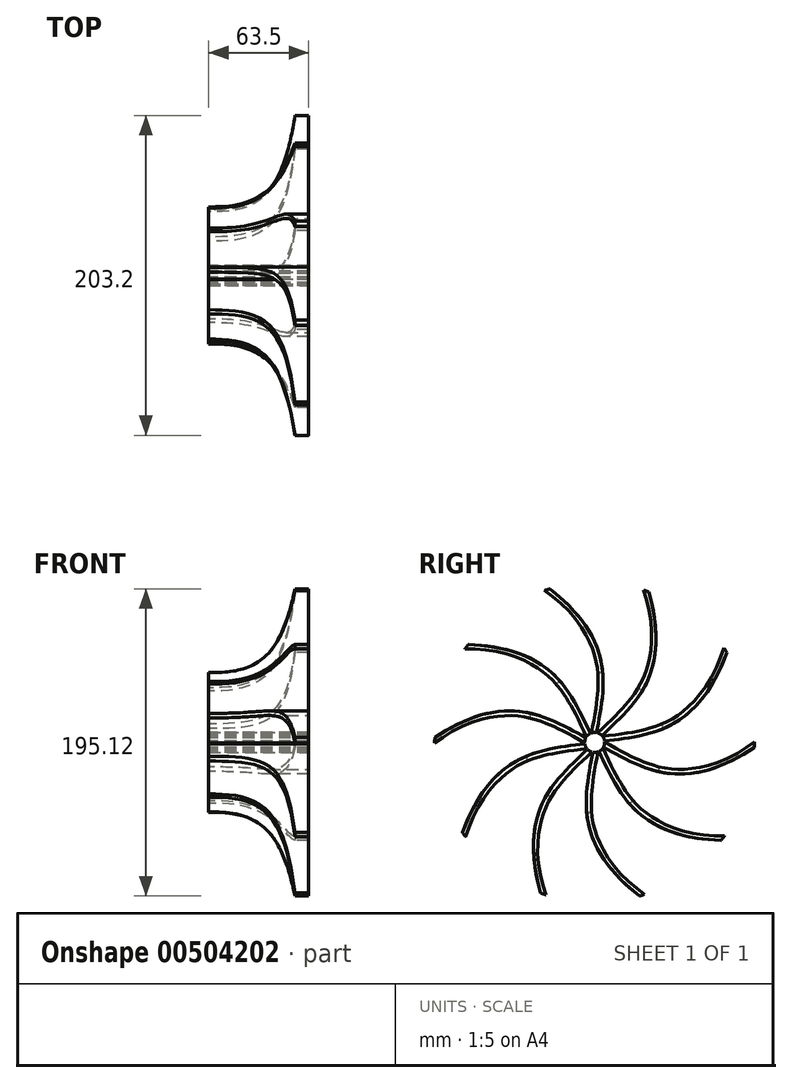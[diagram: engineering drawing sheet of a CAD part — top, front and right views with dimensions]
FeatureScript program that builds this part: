
annotation { "Feature Type Name" : "Feature", "Feature Type Description" : "" }
export const myFeature = defineFeature(function(context is Context, id is Id, definition is map)
    precondition{}
    {
        {
            var Q0;
            Q0=qCreatedBy(makeId("Front.planeOp"),FACE);
            var sketch = newSketch(context, id + "F0", { "sketchPlane" : qUnion([Q0])});
            skLineSegment(sketch, "E0", {"start": v(-7.94, 101.6) * mm, "end": v(-7.94, 12.7) * mm, "construction": true});
            skLineSegment(sketch, "E1", {"start": v(-7.94, 12.7) * mm, "end": v(-73.03, 12.7) * mm, "construction": true});
            skLineSegment(sketch, "E2", {"start": v(-73.03, 12.7) * mm, "end": v(-73.03, 3.17) * mm});
            skLineSegment(sketch, "E3", {"start": v(-73.03, 3.17) * mm, "end": v(0, 3.18) * mm});
            skLineSegment(sketch, "E4", {"start": v(0, 3.18) * mm, "end": v(0, 101.6) * mm});
            skLineSegment(sketch, "E5", {"start": v(0, 101.6) * mm, "end": v(-7.94, 101.6) * mm});
            skLineSegment(sketch, "E6", {"start": v(0, 0) * mm, "end": v(-82.55, 0) * mm, "construction": true});
            skFitSpline(sketch, "E7", {"points": [v(-73.03, 12.7) * mm, v(-28.58, 28.58) * mm, v(-17.46, 44.45) * mm, v(-12.7, 60.33) * mm, v(-7.94, 98.43) * mm], "startDerivative": vector(149.32, 0) * mm, "endDerivative": vector(0, 182.1) * mm});
            skLineSegment(sketch, "E8", {"start": v(-7.94, 98.43) * mm, "end": v(-7.94, 101.6) * mm});
            skSolve(sketch);
        }
        {
            var Q0;
            Q0=sQuery(id+"F0.wireOp",EDGE,"E2");
            var Q1;
            Q1=sQuery(id+"F0.wireOp",EDGE,"E3");
            var Q2;
            Q2=sQuery(id+"F0.wireOp",EDGE,"E4");
            var Q3;
            Q3=sQuery(id+"F0.wireOp",EDGE,"E5");
            var Q4;
            Q4=sQuery(id+"F0.wireOp",EDGE,"E8");
            var Q5;
            Q5=sQuery(id+"F0.wireOp",EDGE,"E7");
            var Q6;
            Q6=sQuery(id+"F0.wireOp",EDGE,"E6");
            revolve(context, id + "F1", {"bodyType" : ToolBodyType.SURFACE, "surfaceEntities" : qUnion([Q0, Q1, Q2, Q3, Q4, Q5]), "axis" : qUnion([Q6]), "revolveType" : RevolveType.FULL});
        }
        {
            var Q0;
            Q0=makeQuery(id+"F1.opRevolve","SWEPT_FACE",FACE,{"disambiguationData":[OSD([sQuery(id+"F0.wireOp",EDGE,"E2")])]});
            cPlane(context, id + "F2", {"entities" : qUnion([Q0]), "cplaneType" : CPlaneType.OFFSET, "offset" : 3.17 * mm, "width" : 152.4 * mm, "height" : 152.4 * mm});
        }
        {
            var Q0;
            Q0=qCreatedBy(id+"F2.planeOp",FACE);
            var sketch = newSketch(context, id + "F3", { "sketchPlane" : qUnion([Q0])});
            skCircle(sketch, "E9.0", {"center": v(0, 0) * mm, "radius": 12.7 * mm, "construction": true});
            skCircle(sketch, "E10.0", {"center": v(0, 0) * mm, "radius": 101.6 * mm, "construction": true});
            skCircle(sketch, "E11.0", {"center": v(0, 0) * mm, "radius": 98.43 * mm, "construction": true});
            skFitSpline(sketch, "E12", {"points": [v(0, 0) * mm, v(5.08, 31.75) * mm, v(-38.1, 104.78) * mm], "startDerivative": vector(12, 75) * mm, "endDerivative": vector(-200.06, 138.5) * mm});
            skLineSegment(sketch, "E13", {"start": v(-130.62, 0) * mm, "end": v(132.26, 0) * mm, "construction": true});
            skLineSegment(sketch, "E14", {"start": v(0, 122.97) * mm, "end": v(0, -146.11) * mm, "construction": true});
            skFitSpline(sketch, "E15.0", {"points": [v(-3.14, 0.5) * mm, v(-2.62, 3.7) * mm, v(-1.68, 8.54) * mm, v(-0.38, 15.22) * mm, v(0.54, 20.39) * mm, v(1.2, 24.86) * mm, v(1.63, 28.57) * mm, v(1.88, 31.4) * mm, v(2.07, 34.32) * mm, v(2.2, 38.27) * mm, v(2.08, 43.36) * mm, v(1.29, 49.7) * mm, v(-0.34, 56.29) * mm, v(-3, 63.16) * mm, v(-8.2, 72.72) * mm, v(-18.41, 85.48) * mm, v(-31.7, 96.48) * mm, v(-39.9, 102.16) * mm]});
            skLineSegment(sketch, "E16", {"start": v(-39.9, 102.16) * mm, "end": v(-38.1, 104.78) * mm});
            skLineSegment(sketch, "E17", {"start": v(-3.14, 0.5) * mm, "end": v(0, 0) * mm});
            skSolve(sketch);
        }
        {
            var Q0;
            Q0=makeQuery(id+"F3.imprint","IMPRINT",FACE,{"disambiguationData":[TD([[makeQuery(id+"F3.imprint","IMPRINT",EDGE,{"derivedFrom":sQuery(id+"F3.wireOp",EDGE,"E12")}),1.0]])]});
            var Q1;
            Q1=makeQuery(id+"F1.opRevolve","SWEPT_FACE",FACE,{"disambiguationData":[OSD([sQuery(id+"F0.wireOp",EDGE,"E8")])]});
            extrude(context, id + "F4", {"entities" : qUnion([Q0]), "endBoundEntityFace" : qUnion([Q1]), "depth" : 63.5 * mm});
        }
        {
            var Q0;
            Q0=qCreatedBy(makeId("Front.planeOp"),FACE);
            var sketch = newSketch(context, id + "F5", { "sketchPlane" : qUnion([Q0])});
            skFitSpline(sketch, "E18.0", {"points": [v(-69.85, 0.5) * mm, v(-69.85, 3.57) * mm, v(-69.85, 8.13) * mm, v(-69.85, 14.4) * mm, v(-69.85, 19.26) * mm, v(-69.85, 24.35) * mm, v(-69.85, 28.86) * mm, v(-69.85, 32.64) * mm, v(-69.85, 36.58) * mm, v(-69.85, 41.79) * mm, v(-69.85, 48.45) * mm, v(-69.85, 57.84) * mm, v(-69.85, 70.48) * mm, v(-69.85, 86.87) * mm, v(-69.85, 98.48) * mm, v(-69.85, 104.42) * mm]});
            skLineSegment(sketch, "E19.0", {"start": v(-6.35, 102.16) * mm, "end": v(-69.85, 102.16) * mm});
            skFitSpline(sketch, "E20", {"points": [v(-73.03, 44.45) * mm, v(-50.8, 46.04) * mm, v(-30.16, 58.74) * mm, v(-17.46, 88.9) * mm, v(-12.7, 117.48) * mm], "startDerivative": vector(83.73, 0) * mm, "endDerivative": vector(18.36, 110.14) * mm});
            skLineSegment(sketch, "E21", {"start": v(-73.03, 44.45) * mm, "end": v(-73.03, 117.47) * mm});
            skLineSegment(sketch, "E22", {"start": v(-73.03, 117.48) * mm, "end": v(-12.7, 117.48) * mm});
            skLineSegment(sketch, "E23", {"start": v(0, 0) * mm, "end": v(-127, 0) * mm, "construction": true});
            skSolve(sketch);
        }
        {
            var Q0;
            {var subQ0=sQuery(id+"F5.wireOp",EDGE,"E19.0");var subQ1=sQuery(id+"F5.wireOp",EDGE,"E18.0");var subQ2=makeQuery(id+"F5.imprint","INTERSECT",VERTEX,{"derivedFrom":[subQ1,subQ0]});Q0=makeQuery(id+"F5.imprint","IMPRINT",FACE,{"disambiguationData":[TD([[makeQuery(id+"F5.imprint","IMPRINT",EDGE,{"disambiguationData":[TD([[subQ2,1.0]])],"derivedFrom":subQ1}),-1.0]])]});}
            var Q1;
            {var subQ4=sQuery(id+"F5.wireOp",EDGE,"E21");Q1=makeQuery(id+"F5.imprint","IMPRINT",FACE,{"disambiguationData":[TD([[makeQuery(id+"F5.imprint","IMPRINT",EDGE,{"derivedFrom":subQ4}),-1.0]])]});}
            var Q2;
            Q2=sQuery(id+"F5.wireOp",EDGE,"E23");
            revolve(context, id + "F6", {"operationType" : NewBodyOperationType.REMOVE, "entities" : qUnion([Q0, Q1]), "axis" : qUnion([Q2]), "revolveType" : RevolveType.FULL, "oppositeDirection" : true});
        }
        {
            var Q0;
            Q0=qCreatedBy(makeId("Front.planeOp"),FACE);
            var sketch = newSketch(context, id + "F7", { "sketchPlane" : qUnion([Q0])});
            skLineSegment(sketch, "E24.bottom", {"start": v(-76.2, 6.35) * mm, "end": v(25.4, 6.35) * mm});
            skLineSegment(sketch, "E24.top", {"start": v(-76.2, 101.6) * mm, "end": v(25.4, 101.6) * mm});
            skLineSegment(sketch, "E24.left", {"start": v(-76.2, 101.6) * mm, "end": v(-76.2, 6.35) * mm});
            skLineSegment(sketch, "E24.right", {"start": v(25.4, 101.6) * mm, "end": v(25.4, 6.35) * mm});
            skLineSegment(sketch, "E25", {"start": v(0, 0) * mm, "end": v(-101.6, 0) * mm, "construction": true});
            skSolve(sketch);
        }
        {
            var Q0;
            Q0=makeQuery(id+"F7.imprint","IMPRINT",FACE,{"disambiguationData":[TD([[makeQuery(id+"F7.imprint","IMPRINT",EDGE,{"derivedFrom":sQuery(id+"F7.wireOp",EDGE,"E24.bottom")}),1.0]])]});
            var Q1;
            Q1=sQuery(id+"F7.wireOp",EDGE,"E25");
            revolve(context, id + "F8", {"operationType" : NewBodyOperationType.INTERSECT, "entities" : qUnion([Q0]), "axis" : qUnion([Q1]), "revolveType" : RevolveType.FULL});
        }
        {
            var Q0;
            Q0=makeQuery(id+"F4.opExtrude","SWEPT_BODY",BODY,{"disambiguationData":[OSD([sQuery(id+"F3.wireOp",EDGE,"E12"),sQuery(id+"F3.wireOp",EDGE,"E15.0"),sQuery(id+"F3.wireOp",EDGE,"E16"),sQuery(id+"F3.wireOp",EDGE,"E17")])]});
            var Q1;
            Q1=sQuery(id+"F7.wireOp",EDGE,"E25");
            circularPattern(context, id + "F9", {"entities" : qUnion([Q0]), "axis" : qUnion([Q1]), "angle" : 360 * degree, "instanceCount" : 10, "equalSpace" : true});
        }
    });
